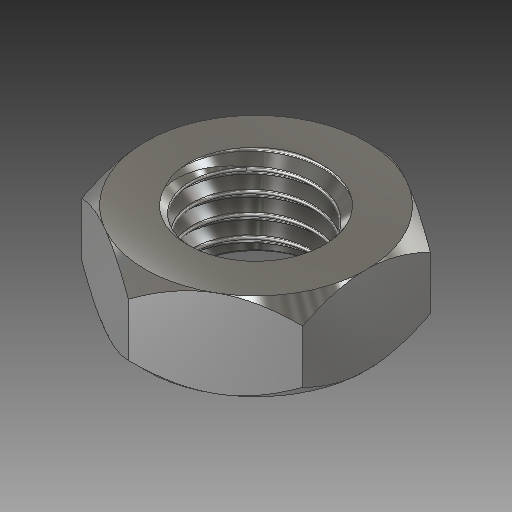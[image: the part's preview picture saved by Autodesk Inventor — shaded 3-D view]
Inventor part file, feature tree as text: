
AUTODESK INVENTOR PART (.ipt)
format: ipt  version: 2019 (Build 230136000, 136)  size: 508,928 bytes
history: native  units: mm
features: sketch x5, extrude x4, chamfer x1, helix x1, fillet x1
ambient origin geometry x8: Origin, YZ Plane, XZ Plane, XY Plane, X Axis, Y Axis, Z Axis, Center Point
bodies: Solid1 (feature_tree)
feature tree (12):
  extrude  "Extrusion1"  Depth=7.5mm TaperAngle=0.0deg
  extrude  "Extrusion2"  Depth=7.5mm TaperAngle=45.0deg
  extrude  "Extrusion3"  Depth=7.5mm TaperAngle=0.0deg
  extrude  "Extrusion4"  Depth=1.7mm
  chamfer  "Chamfer1"  Distance=0.2mm
  helix  "Coil1"  [1 undecoded]
  fillet  "Fillet1"  Radius=1.0mm
  sketch  "Sketch1"  dims[d0=19.0mm d1=7.5mm d2=0.0mm]
  sketch  "Sketch2"  dims[d3=7.5mm d4=45.0deg d5=7.5mm d6=45.0deg]
  sketch  "Sketch3"  dims[d7=9.728mm d8=7.5mm d9=0.0mm]
  sketch  "Sketch4"  dims[d10=1.0mm d11=2.0mm d12=45.0deg d13=1.7mm]
  sketch  "Sketch5"  dims[d14=60.0deg d15=0.2mm d16=4.864mm d17=1.0mm d18=1.7mm d19=12.0mm d20=10.0mm d21=0.0mm d22=90.0deg d23=90.0deg d24=0.0mm d25=0.0mm d26=0.2mm]
note: 1 required parameter value undecoded (feature->parameter linkage not recoverable at this tier; creation-order binding heuristic only, values carry confidence <= 0.55)
